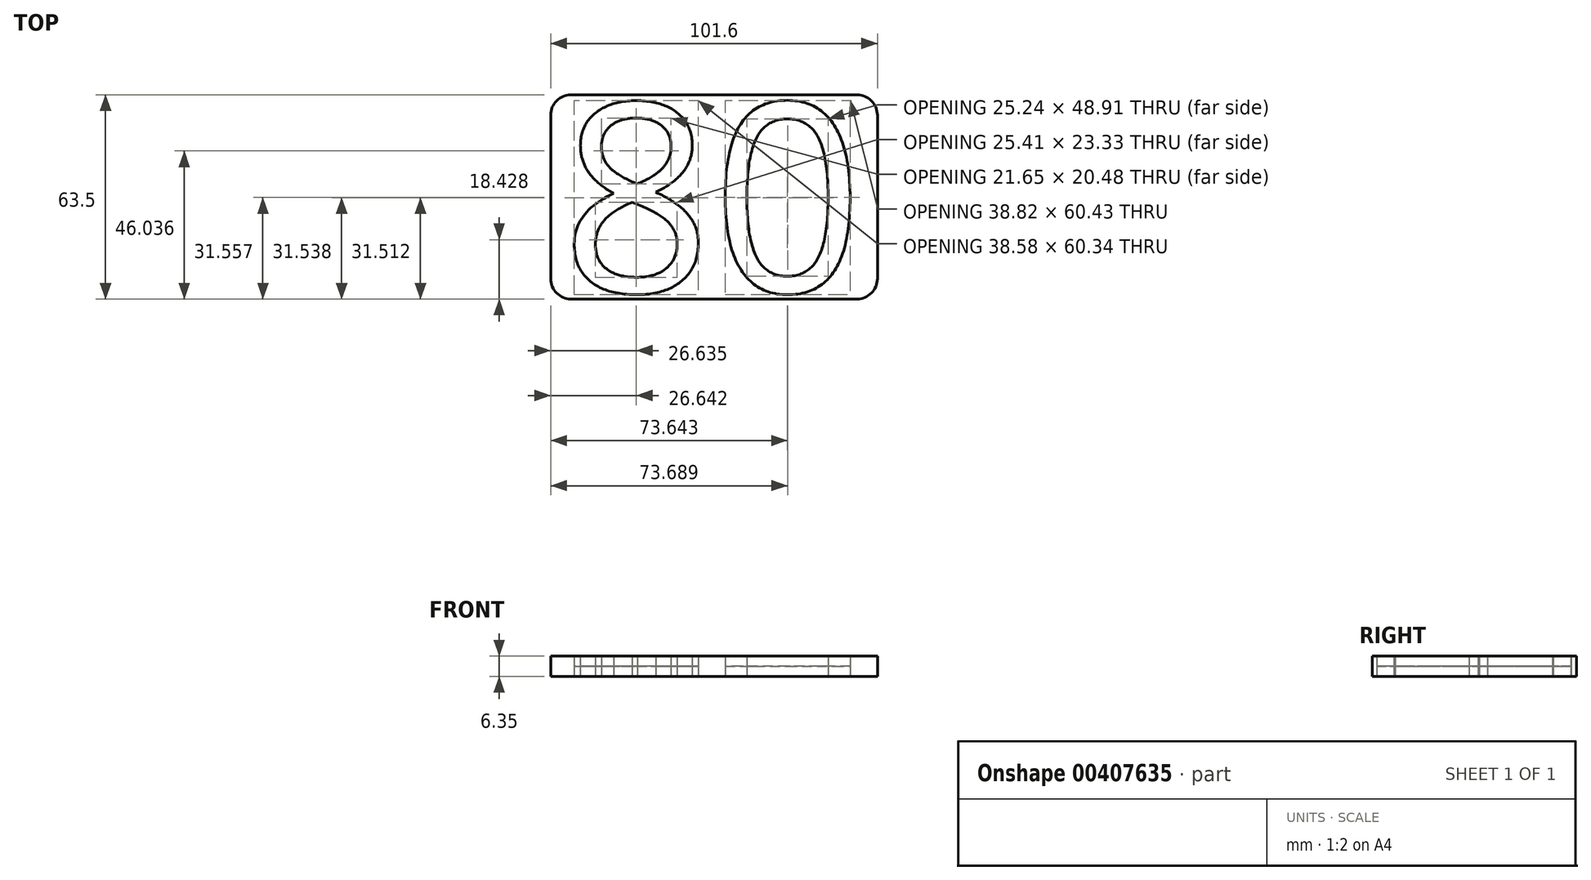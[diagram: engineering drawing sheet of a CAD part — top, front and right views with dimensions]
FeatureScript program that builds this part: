
annotation { "Feature Type Name" : "Feature", "Feature Type Description" : "" }
export const myFeature = defineFeature(function(context is Context, id is Id, definition is map)
    precondition{}
    {
        {
            var Q0;
            Q0=qCreatedBy(makeId("Top.planeOp"),FACE);
            var sketch = newSketch(context, id + "F0", { "sketchPlane" : qUnion([Q0])});
            skText(sketch, "E0", { "text": "80\n", "fontName": "OpenSans-Regular.ttf"});
            skLineSegment(sketch, "E1.bottom", {"start": v(-44.45, 31.75) * mm, "end": v(44.45, 31.75) * mm});
            skLineSegment(sketch, "E1.top", {"start": v(-44.45, -31.75) * mm, "end": v(44.45, -31.75) * mm});
            skLineSegment(sketch, "E1.left", {"start": v(-50.8, 25.4) * mm, "end": v(-50.8, -25.4) * mm});
            skLineSegment(sketch, "E1.right", {"start": v(50.8, 25.4) * mm, "end": v(50.8, -25.4) * mm});
            skPoint(sketch, "E1.middle", {"position": v(0, 0) * mm});
            skPoint(sketch, "E2.visualSharp", {"position": v(-50.8, 31.75) * mm});
            skArc(sketch, "E2.filletArc", {"start": v(-44.45, 31.75) * mm, "mid": v(-48.94, 29.9) * mm, "end": v(-50.8, 25.4) * mm});
            skPoint(sketch, "E3.visualSharp", {"position": v(50.8, 31.75) * mm});
            skArc(sketch, "E3.filletArc", {"start": v(50.8, 25.4) * mm, "mid": v(48.94, 29.9) * mm, "end": v(44.45, 31.75) * mm});
            skPoint(sketch, "E4.visualSharp", {"position": v(50.8, -31.75) * mm});
            skArc(sketch, "E4.filletArc", {"start": v(44.45, -31.75) * mm, "mid": v(48.94, -29.9) * mm, "end": v(50.8, -25.4) * mm});
            skPoint(sketch, "E5.visualSharp", {"position": v(-50.8, -31.75) * mm});
            skArc(sketch, "E5.filletArc", {"start": v(-50.8, -25.4) * mm, "mid": v(-48.94, -29.9) * mm, "end": v(-44.45, -31.75) * mm});
            const initialGuessF0  = {"E0": [-0.04763, -0.0296, 1, 0, 0.0592]};
            skSetInitialGuess(sketch, initialGuessF0);
            skSolve(sketch);
        }
        {
            var Q0;
            Q0=makeQuery(id+"F0.imprint","IMPRINT",FACE,{"disambiguationData":[TD([[makeQuery(id+"F0.imprint","IMPRINT",EDGE,{"derivedFrom":sQuery(id+"F0.wireOp",EDGE,"E0.sketch_text.stroke-0")}),1.0]])]});
            var Q1;
            Q1=makeQuery(id+"F0.imprint","IMPRINT",FACE,{"disambiguationData":[TD([[makeQuery(id+"F0.imprint","IMPRINT",EDGE,{"derivedFrom":sQuery(id+"F0.wireOp",EDGE,"E0.sketch_text.stroke-23")}),1.0]])]});
            var Q2;
            Q2=makeQuery(id+"F0.imprint","IMPRINT",FACE,{"disambiguationData":[TD([[makeQuery(id+"F0.imprint","IMPRINT",EDGE,{"derivedFrom":sQuery(id+"F0.wireOp",EDGE,"E0.sketch_text.stroke-15")}),1.0]])]});
            var Q3;
            Q3=makeQuery(id+"F0.imprint","IMPRINT",FACE,{"disambiguationData":[TD([[makeQuery(id+"F0.imprint","IMPRINT",EDGE,{"derivedFrom":sQuery(id+"F0.wireOp",EDGE,"E0.sketch_text.stroke-39")}),1.0]])]});
            extrude(context, id + "F1", {"entities" : qUnion([Q0, Q1, Q2, Q3]), "depth" : 6.35 * mm});
        }
        {
            var Q0;
            Q0=makeQuery(id+"F0.imprint","IMPRINT",FACE,{"disambiguationData":[TD([[makeQuery(id+"F0.imprint","IMPRINT",EDGE,{"derivedFrom":sQuery(id+"F0.wireOp",EDGE,"E0.sketch_text.stroke-0")}),-1.0]])]});
            var Q1;
            Q1=makeQuery(id+"F0.imprint","IMPRINT",FACE,{"disambiguationData":[TD([[makeQuery(id+"F0.imprint","IMPRINT",EDGE,{"derivedFrom":sQuery(id+"F0.wireOp",EDGE,"E0.sketch_text.stroke-31")}),-1.0]])]});
            extrude(context, id + "F2", {"entities" : qUnion([Q0, Q1]), "depth" : 3.17 * mm});
        }
    });
